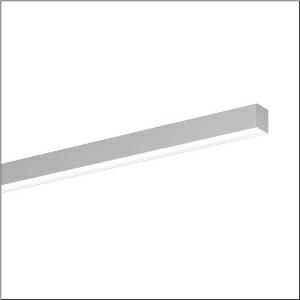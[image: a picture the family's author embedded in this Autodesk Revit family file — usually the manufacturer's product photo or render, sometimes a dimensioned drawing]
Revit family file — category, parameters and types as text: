
# Revit family: silica_r__21_51mx20dc35sb_d3c3
name_source: partatom
category: Lighting Fixtures
units: mm (PartAtom-declared; Revit-internal decimal feet)

## family parameters
Cut with Voids When Loaded = No
Host = Face
Light Source = No
Part Type = Normal
Room Calculation Point = No
Round Connector Dimension = Use Diameter
Shared = No

## types (1)
- --- (1 x LED, 6000 lm, 42.6 W, 3000K)
    Apparent Load = 43 VA
    CIE Flux Codes = 48 79 96 100 100
    Color Rendering = 80
    Color Temperature = 3000K
    Default Elevation = 1800 mm
    Description = Silica® 21, office luminaire, primary optical cover: cover, of PMMA, opal, light emission: direct distribution, primary light characteristic: symmetric, installation type: surface-mounted, LED, rated luminous flux: 6.000lm, luminous efficacy: 141lm/W, light colour: 830, colour temperature: 3000K, control gear: DALI 2, with terminal, 3+2-pole, max. 2.5mm², mains connection: 220..240V, AC, 50/60Hz, rated input power: 42.6W, luminaire housing, of aluminium, metallic grey (RAL 9006), length: 3.004mm, width: 53mm, height: 53mm, protection rating (complete): IP20, insulation class (complete): insulation class I (protective earthing), certification: CE, permissible operating ambient temperature: 0..+35°C, standard: EN 50419, packaging unit: 1 piece
    Height = 53 mm
    Lamp = 1 x LED
    Lamp Light Flux = 6000 lm
    Lamp Power = 42.6 W
    Lamp count = 1
    Length = 3004 mm
    Luminous efficacy = 141 lm/W
    Manufacturer = Siteco
    ModVariant = No
    Model = 51MX20DC35SB
    Mounting Place = Ceiling
    Mounting Type = Surface mounted
    Number of Poles = 1
    OnlyDefault = Yes
    Power Factor = 1
    Product Name = Silica® 21
    Product group = office luminaire | ceiling mounted
    ProductGroupID = 302
    Protection Class = Protection class I
    Protection Degree = IP 20
    RLX_Detail_Level = 1
    RLX_Emergency_Light_Flux = 0 lm
    RLX_Emergency_Type = 0
    RLX_Emergency_Type_DB = No
    RlxData = <blob elided: 26381 chars, md5=9e451191>
    Socket = socket
    Standby Power = 0 W
    System Light Flux = 6000 lm
    System Power = 43 W
    Type Comments = factory setting: luminous flux: 100 % | dim-lin: 254 | 233 mA
    Type Image = l_1335933.jpg
    URL = http://relux.com
    VarID = @adj_117718
    Voltage = 0 V
    Weight = 0.00 kg
    Width = 53 mm

## geometry (parser evidence)
native form markers: Blend x4, Sweep x9
no freeform markers — native parametric forms only
